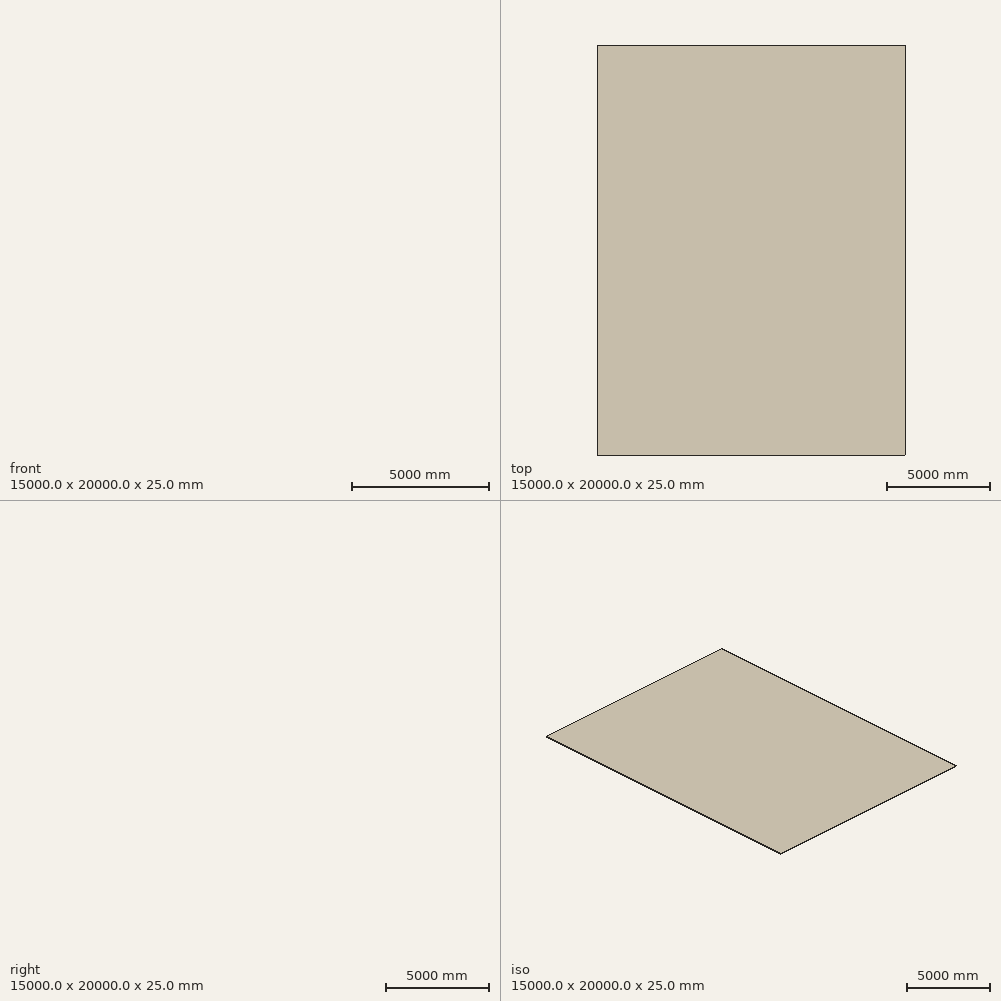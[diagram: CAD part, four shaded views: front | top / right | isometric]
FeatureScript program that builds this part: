
annotation { "Feature Type Name" : "Feature", "Feature Type Description" : "" }
export const myFeature = defineFeature(function(context is Context, id is Id, definition is map)
    precondition{}
    {
        {
            var Q0;
            Q0=qCreatedBy(makeId("Top.planeOp"),FACE);
            var sketch = newSketch(context, id + "F0", { "sketchPlane" : qUnion([Q0])});
            skLineSegment(sketch, "E0.bottom", {"start": v(0, 0) * mm, "end": v(-15000, 0) * mm});
            skLineSegment(sketch, "E0.top", {"start": v(0, 20000) * mm, "end": v(-15000, 20000) * mm});
            skLineSegment(sketch, "E0.left", {"start": v(0, 0) * mm, "end": v(0, 20000) * mm});
            skLineSegment(sketch, "E0.right", {"start": v(-15000, 0) * mm, "end": v(-15000, 20000) * mm});
            skSolve(sketch);
        }
        {
            var Q0;
            Q0=makeQuery(id+"F0.imprint","IMPRINT",FACE,{"disambiguationData":[TD([[makeQuery(id+"F0.imprint","IMPRINT",EDGE,{"derivedFrom":sQuery(id+"F0.wireOp",EDGE,"E0.bottom")}),-1.0]])]});
            extrude(context, id + "F1", {"entities" : qUnion([Q0]), "depth" : 25 * mm, "offsetDistance" : 25 * mm});
        }
    });
